# Revit family: equip-water-cooler-hlsy-tylr-hvrv2-bi-lv-hthb-vrc
name_source: partatom
category: Plumbing Fixtures
units: mm (PartAtom-declared; Revit-internal decimal feet)

## family parameters
Always vertical = Yes
Cut with Voids When Loaded = No
OmniClass Number = 23.45.00.00
OmniClass Title = Sanitary, Laundry, and Cleaning Equipment
Part Type = Normal
Room Calculation Point = No
Round Connector Dimension = Use Radius
Shared = No
Work Plane-Based = No

## types (4) — shared parameters
Activation = -
Apparent Load Phase 1 = 0 VA
BL Replacement Left = -
BL Replacement Right = -
Basin Material = Metal - Steel - Stainless - Chrome
Bubbler = -
Button Material = Plastic - Brown
CW Connection = Yes
Cooler Depth = 1' - 6 5/8"
Cooler Rear Panel Depth = 0' - 6 27/32"
Cooler Width = 1' - 6 1/16"
Description = Mechanical pushbar actuated water cooler
Dispenser Depth = 0' - 8"
Dispenser Height = 2' - 9 9/16"
Glass Filter = -
HW Connection = No
Lower Cooler Bottom = 1' - 0 3/8"
Lower Cooler Height = 1' - 8 5/8"
Lower Orifice Height = 2' - 9"
Manufacturer = Halsey Taylor
Number of Poles = 1
Orifice to Rim = 0' - 1 13/16"
Panel Material = Metal - Steel - Stainless - Color 1
Power Factor = 1
Refrigerated = Yes
Rim to Dispenser = 0' - 4 1/8"
Sanitary Sewer Radius = 0' - 0 5/8"
Specification URL = http://www.halseytaylor.com
Type = Bi-level
URL = www.halseytaylor.com
Upper Cooler Bottom = 1' - 6 7/8"
Upper Cooler Height = 1' - 8 5/8"
Upper Orifice Height = 3' - 3 1/2"
Upper Rim Height = 3' - 1 11/16"
Vent Connection = No
Version = 1.0.0.1
Voltage = 0 V
Volts/Hertz = 115v/60hZ
Waste Connection = Yes
Water Service Flow = 0 GPM
Water Service Size Radius = 0' - 0 1/4"

## per-type parameters (varying)
| type | Filter |
| HTHBHVR8BL | Yes |
| HTHBHVR8BL-NF | NF |
| HTHBHVRBL | Yes |
| HTHBHVRBL-NF | NF |

note: column(s) folded — value = type name in every type: Model

## geometry (parser evidence)
native form markers: Sweep x7
no freeform markers — native parametric forms only
